# Revit family: Grohe_ShowerSystemWithDiverter_269802431
name_source: partatom
category: Plumbing Fixtures
units: mm (PartAtom-declared; Revit-internal decimal feet)

## family parameters
Cut with Voids When Loaded = No
Host = Face
OmniClass Number = 23.45.05.00
OmniClass Title = Sanitary Equipment
Part Type = Normal
Room Calculation Point = No
Round Connector Dimension = Use Diameter
Shared = No

## types (1)
- Shower System With Diverter (269802431)
    Assembly Code = D2013
    AssetType = Fixed
    BIMObjectName = Grohe_ShowerSystemWithDiverter_269802431
    CO2NeutralProduction = GROHE is one of the first leading manufacturer within the sanitary industry having a CO2-neutral production.
    ClassificationName = Uniclass2015
    ClassificationValue = Pr_40_20_87_55
    Color = Grohe_Chrome
    Cost = 0 $
    Default Elevation = 0 mm  [stored 0 ft]
    Description = Shower System With Diverter
    DimensionsDocumentLink = https://cdn.cloud.grohe.com
    DocumentationCertificates = https://www.bimstore.co
    DocumentationInstallationGuide = https://www.bimstore.co
    DocumentationLiterature = https://www.bimstore.co
    DocumentationMaintenance = https://www.bimstore.co
    DocumentationTechnical = https://www.bimstore.co
    DurationUnit = Years
    EF000008 = 0 mm  [stored 0 ft]
    EF000040 = 0 mm  [stored 0 ft]
    EF000049 = 0 mm  [stored 0 ft]
    EF000551 = 0 mm  [stored 0 ft]
    EF000634 = 0.0 Pa
    EF001707 = 0 °C
    EF002169 = Aluminium/plastic
    EF002286 = Insert (push coupling)
    EF002671 = Black
    EF003454 = false
    EF003829 = false
    EF005084 = Wall
    EF006009 = true
    EF006013 = false
    EF006974 = Thermostatic
    EF020103 = false
    EF020785 = M26 x 1.5
    EF021457 = false
    EF021607 = true
    EF021720 = true
    EF021760 = true
    EF022168 = TRUE
    EF022284 = false
    EF023051 = Mechanical
    EF023061 = 0.0 Pa
    EF023686 = Other
    EF023957 = TRUE
    EF024792 = false
    EF024885 = true
    EF024921 = true
    EF025090 = false
    EF025091 = false
    EF025092 = 0
    EF025093 = not applicable
    EF025094 = 0
    EF025095 = not applicable
    EF025096 = true
    EFSE0002 = true
    Ecojoy = No
    ExpectedLife = 0
    FaucetMaterial = Grohe-Chrome
    Finish = Chrome
    FullRecyclabilityOfPlastic = All plastic components are fully recycable
    GROHESocialCommittment = green.grohe.com/social_engagement
    GROHESustainability = green.grohe.com
    IfcExportAs = IfcPipeFitting
    IfcExportType = IfcPipeFittingType
    Keynote = N16
    Manufacturer = Grohe
    ManufacturerName = Grohe
    Model = Shower System With Diverter
    ModelNumber = 269802431
    ModelReference = Shower System With Diverter
    NBSDescription = Shower fittings package
    NBSObjectName = Grohe - Shower fittings package
    NBSReference = 45-35-70/321
    NominalDepth = 0 mm  [stored 0 ft]
    NominalHeight = 0 mm  [stored 0 ft]
    NominalLength = 0 mm  [stored 0 ft]
    PrimaryMaterial = Grohe_Chrome
    ProductDescription = consisting of:

horizontal 390 mm shower arm, adjustable before installation (14 047)

change by diverter between hand shower, head shower or head shower Eco setting

head shower Tempesta 250 (26 666)

spray pattern: Rain

head shower with white rear cover

with ball joint, rotation angle ± 10°

hand shower Tempesta 110 (28 419)

3 spray patterns: Rain, Jet, Massage

adjustable in height with gliding element

distance between diverter and upper bracket: 920 mm

Rotaflex TwistStop shower hose 1750 mm 1/2" x 1/2" (28 410)

diverter + 620 mm rail (26 381)

flexible installation: connection to faucet / wall union for water supply with 1/2" thread of the 500 mm shower hose

maximum flow rate (at 3 bar): 8.7 l/min

GROHE SmartSwitch - easily rotate the dial to enjoy your preferred spray option

GROHE DreamSpray perfect spray pattern

ShockProof silicone ring prevents damages caused by shower falling

GROHE Long-Life finish

SpeedClean anti-limescale system

Inner WaterGuide for a longer life

suitable for instantaneous heaters from 18 kW/h

minimum flow rate 7 l/min

min. recommended pressure 1.0 bar

professional exclusive
    ProductNumber = 269802431
    ProductShortText = Flex shower system with diverter for wall mounting
    ProductType = Shower System
    ProductionYear = 2023
    SustainabilityAward = green.grohe.com/awards
    SustainabilityReport = green.grohe.com/reporting
    TPIDocumentLink = https://cdn.cloud.grohe.com
    Type Comments = Shower System With Diverter
    TypeName = Shower System With Diverter
    URL = https://www.grohe.co.uk
    WarrantyDurationLabor = 0
    WarrantyDurationParts = 0
    WarrantyDurationUnit = Years
    _BSBibleVersion = 17
    _BimSpecGuid = 0
    _CurrentRevision = 1
    _DistributedBy = https://www.bimstore.co
    _ObjectUserGuide = https://www.bimstore.co

note: [stored X ft] marks values corroborated as IEEE doubles in the binary element streams (Revit-internal decimal feet)

## geometry (parser evidence)
native form markers: Sweep x3
no freeform markers — native parametric forms only
